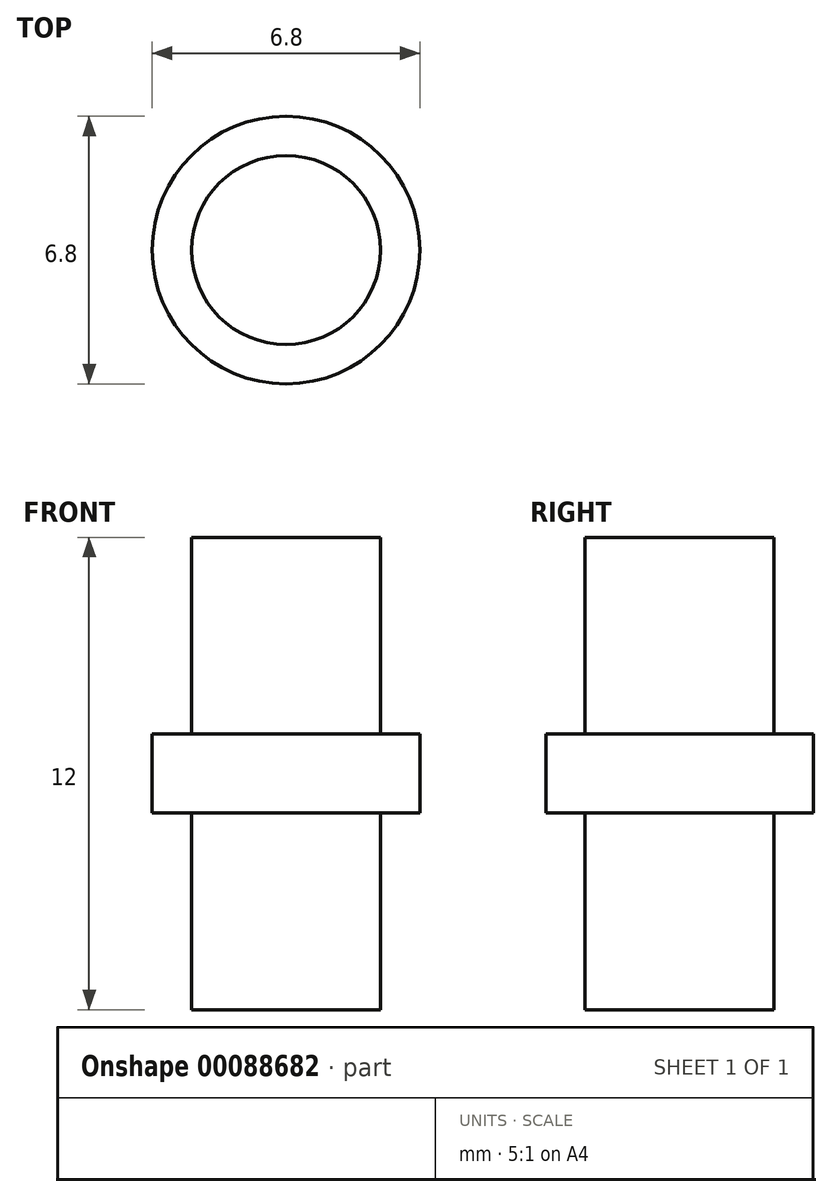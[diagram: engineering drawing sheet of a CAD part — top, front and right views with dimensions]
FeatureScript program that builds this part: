
annotation { "Feature Type Name" : "Feature", "Feature Type Description" : "" }
export const myFeature = defineFeature(function(context is Context, id is Id, definition is map)
    precondition{}
    {
        {
            var Q0;
            Q0=qCreatedBy(makeId("Front.planeOp"),FACE);
            var sketch = newSketch(context, id + "F0", { "sketchPlane" : qUnion([Q0])});
            skLineSegment(sketch, "E0", {"start": v(0, 0) * mm, "end": v(0, 6) * mm, "construction": true});
            skLineSegment(sketch, "E1", {"start": v(0, 6) * mm, "end": v(2.4, 6) * mm});
            skLineSegment(sketch, "E2", {"start": v(2.4, 6) * mm, "end": v(2.4, 1) * mm});
            skLineSegment(sketch, "E3", {"start": v(2.4, 1) * mm, "end": v(3.4, 1) * mm});
            skLineSegment(sketch, "E4", {"start": v(3.4, 1) * mm, "end": v(3.4, 0) * mm});
            skLineSegment(sketch, "E5", {"start": v(0, 6) * mm, "end": v(0, 0) * mm});
            skLineSegment(sketch, "E6.MirrorCS", {"start": v(0, -6) * mm, "end": v(0, 0) * mm});
            skLineSegment(sketch, "E7.MirrorCS", {"start": v(0, -6) * mm, "end": v(2.4, -6) * mm});
            skLineSegment(sketch, "E8.MirrorCS", {"start": v(2.4, -6) * mm, "end": v(2.4, -1) * mm});
            skLineSegment(sketch, "E9.MirrorCS", {"start": v(2.4, -1) * mm, "end": v(3.4, -1) * mm});
            skLineSegment(sketch, "E10.MirrorCS", {"start": v(3.4, -1) * mm, "end": v(3.4, 0) * mm});
            skSolve(sketch);
        }
        {
            var Q0;
            Q0=makeQuery(id+"F0.imprint","IMPRINT",FACE,{"disambiguationData":[TD([[makeQuery(id+"F0.imprint","IMPRINT",EDGE,{"derivedFrom":sQuery(id+"F0.wireOp",EDGE,"E1")}),-1.0]])]});
            var Q1;
            Q1=sQuery(id+"F0.wireOp",EDGE,"E5");
            revolve(context, id + "F1", {"entities" : qUnion([Q0]), "axis" : qUnion([Q1]), "revolveType" : RevolveType.FULL});
        }
    });
